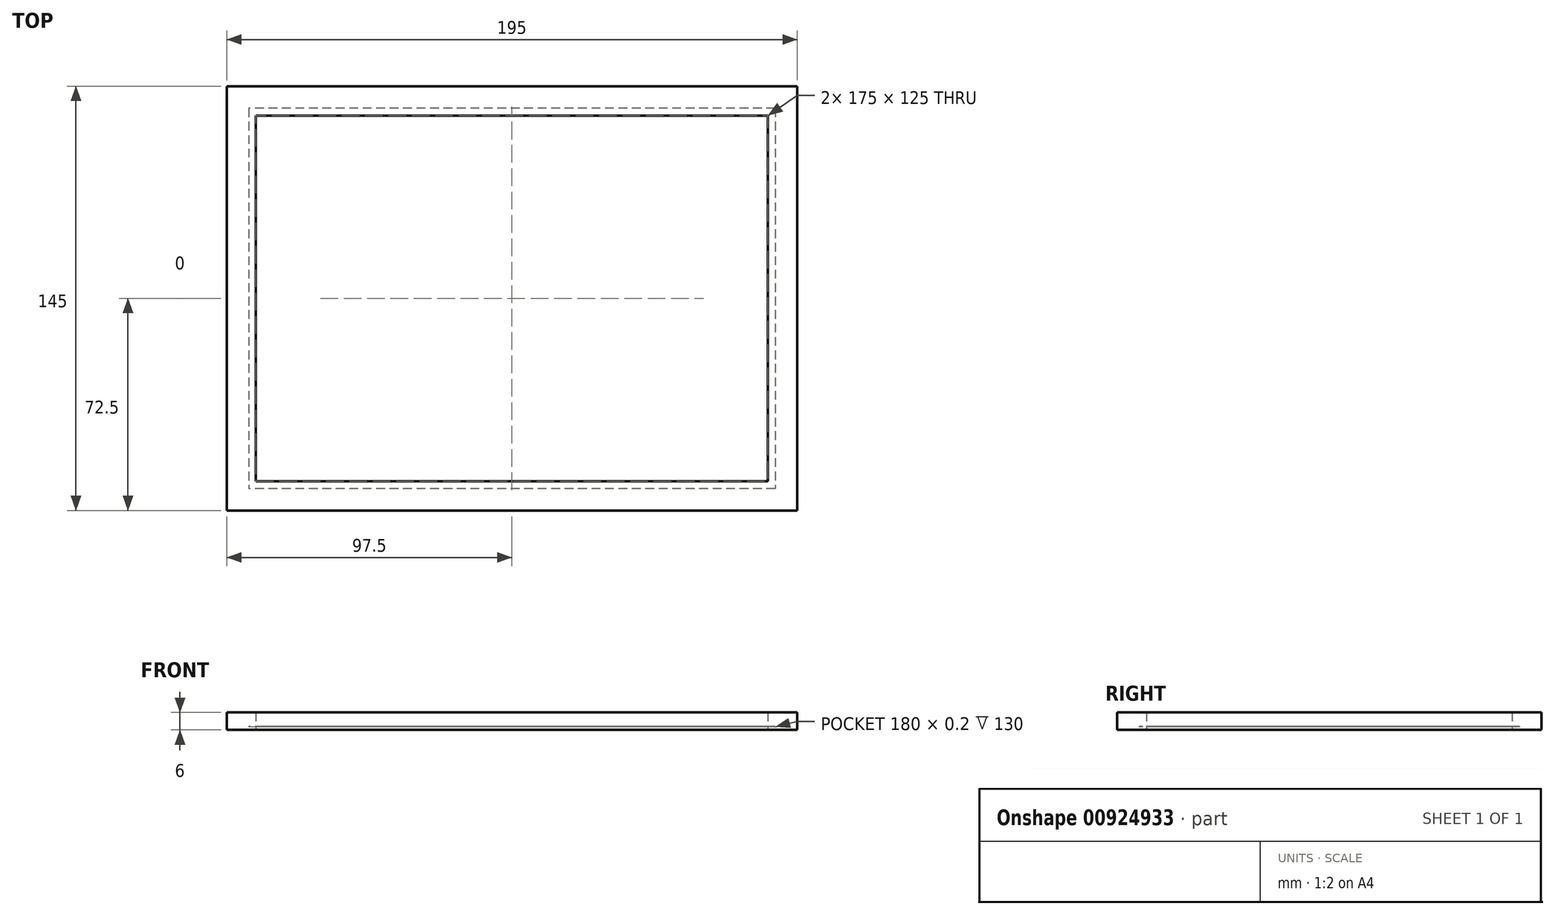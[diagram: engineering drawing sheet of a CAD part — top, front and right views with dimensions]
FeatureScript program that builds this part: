
annotation { "Feature Type Name" : "Feature", "Feature Type Description" : "" }
export const myFeature = defineFeature(function(context is Context, id is Id, definition is map)
    precondition{}
    {
        {
            var Q0;
            Q0=qCreatedBy(makeId("Top.planeOp"),FACE);
            var sketch = newSketch(context, id + "F0", { "sketchPlane" : qUnion([Q0])});
            skLineSegment(sketch, "E0.bottom", {"start": v(90, 65) * mm, "end": v(-90, 65) * mm});
            skLineSegment(sketch, "E0.top", {"start": v(90, -65) * mm, "end": v(-90, -65) * mm});
            skLineSegment(sketch, "E0.left", {"start": v(90, 65) * mm, "end": v(90, -65) * mm});
            skLineSegment(sketch, "E0.right", {"start": v(-90, 65) * mm, "end": v(-90, -65) * mm});
            skPoint(sketch, "E0.middle", {"position": v(0, 0) * mm});
            skLineSegment(sketch, "E1.bottom", {"start": v(97.5, 72.5) * mm, "end": v(-97.5, 72.5) * mm});
            skLineSegment(sketch, "E1.top", {"start": v(97.5, -72.5) * mm, "end": v(-97.5, -72.5) * mm});
            skLineSegment(sketch, "E1.left", {"start": v(97.5, 72.5) * mm, "end": v(97.5, -72.5) * mm});
            skLineSegment(sketch, "E1.right", {"start": v(-97.5, 72.5) * mm, "end": v(-97.5, -72.5) * mm});
            skLineSegment(sketch, "E2.bottom", {"start": v(87.5, 62.5) * mm, "end": v(-87.5, 62.5) * mm});
            skLineSegment(sketch, "E2.top", {"start": v(87.5, -62.5) * mm, "end": v(-87.5, -62.5) * mm});
            skLineSegment(sketch, "E2.left", {"start": v(87.5, 62.5) * mm, "end": v(87.5, -62.5) * mm});
            skLineSegment(sketch, "E2.right", {"start": v(-87.5, 62.5) * mm, "end": v(-87.5, -62.5) * mm});
            skSolve(sketch);
        }
        {
            var Q0;
            Q0=makeQuery(id+"F0.imprint","IMPRINT",FACE,{"disambiguationData":[TD([[makeQuery(id+"F0.imprint","IMPRINT",EDGE,{"derivedFrom":sQuery(id+"F0.wireOp",EDGE,"E0.bottom")}),-1.0]])]});
            var Q1;
            Q1=makeQuery(id+"F0.imprint","IMPRINT",FACE,{"disambiguationData":[TD([[makeQuery(id+"F0.imprint","IMPRINT",EDGE,{"derivedFrom":sQuery(id+"F0.wireOp",EDGE,"E0.bottom")}),1.0]])]});
            extrude(context, id + "F1", {"entities" : qUnion([Q0, Q1]), "depth" : 5 * mm, "offsetDistance" : 25 * mm});
        }
        {
            var Q0;
            Q0=makeQuery(id+"F0.imprint","IMPRINT",FACE,{"disambiguationData":[TD([[makeQuery(id+"F0.imprint","IMPRINT",EDGE,{"derivedFrom":sQuery(id+"F0.wireOp",EDGE,"E0.bottom")}),1.0]])]});
            var Q1;
            Q1=makeQuery(id+"F0.imprint","IMPRINT",FACE,{"disambiguationData":[TD([[makeQuery(id+"F0.imprint","IMPRINT",EDGE,{"derivedFrom":sQuery(id+"F0.wireOp",EDGE,"E0.bottom")}),-1.0]])]});
            extrude(context, id + "F2", {"entities" : qUnion([Q0, Q1]), "operationType" : NewBodyOperationType.ADD, "oppositeDirection" : true, "depth" : 1 * mm, "offsetDistance" : 25 * mm});
        }
        {
            var Q0;
            Q0=makeQuery(id+"F0.imprint","IMPRINT",FACE,{"disambiguationData":[TD([[makeQuery(id+"F0.imprint","IMPRINT",EDGE,{"derivedFrom":sQuery(id+"F0.wireOp",EDGE,"E0.bottom")}),1.0]])]});
            extrude(context, id + "F3", {"entities" : qUnion([Q0]), "operationType" : NewBodyOperationType.REMOVE, "depth" : 0.2 * mm, "offsetDistance" : 25 * mm});
        }
    });
